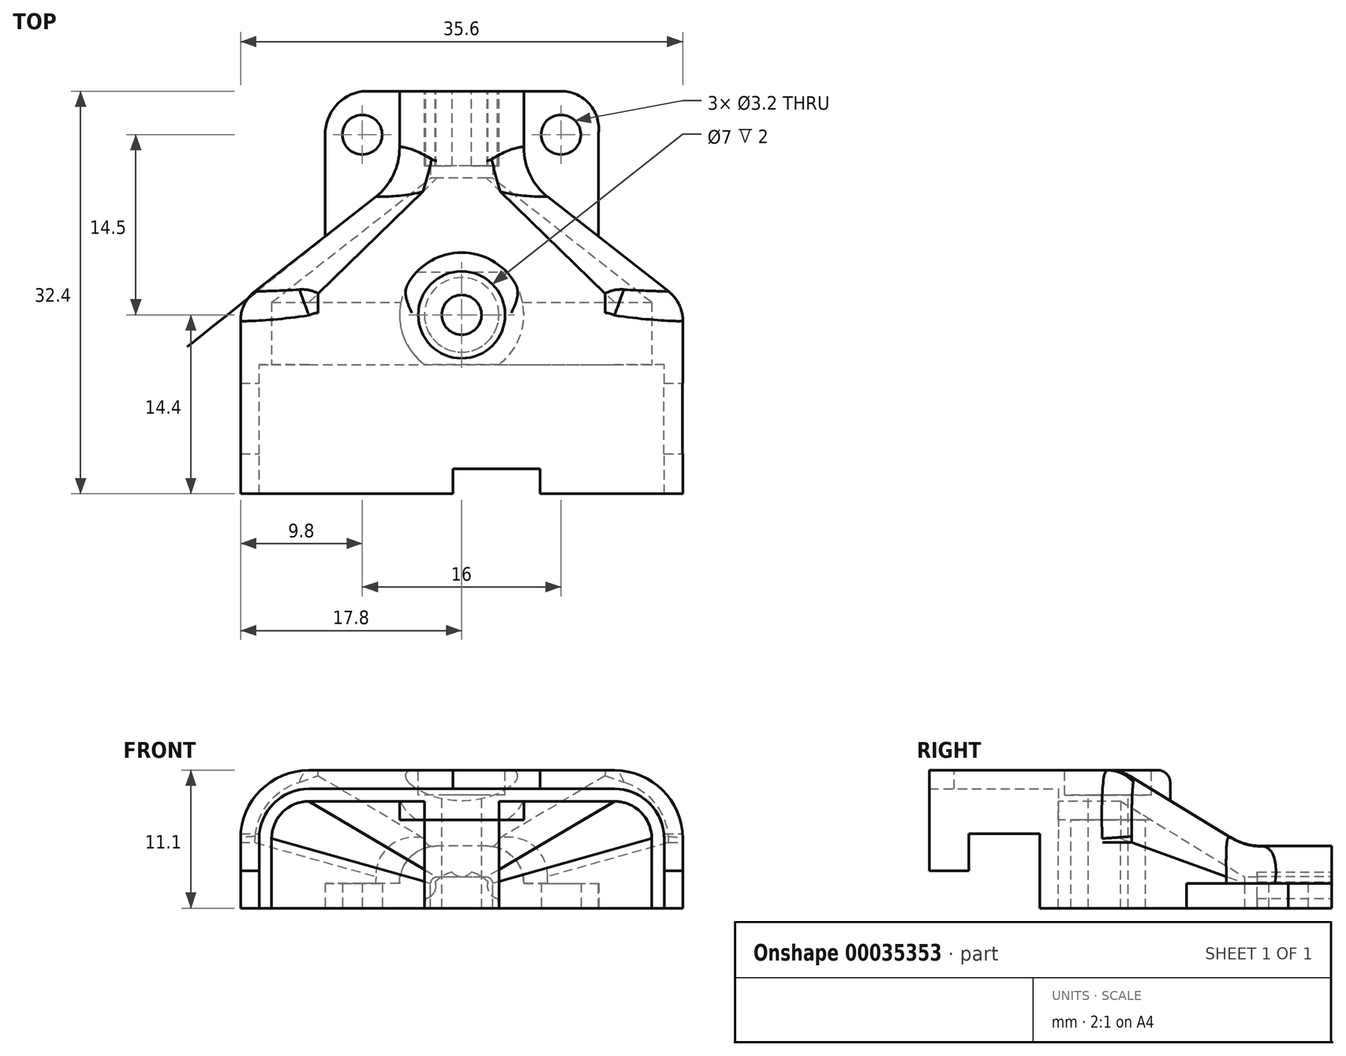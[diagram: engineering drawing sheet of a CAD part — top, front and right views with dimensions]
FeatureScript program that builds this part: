
annotation { "Feature Type Name" : "Feature", "Feature Type Description" : "" }
export const myFeature = defineFeature(function(context is Context, id is Id, definition is map)
    precondition{}
    {
        {
            var Q0;
            Q0=qCreatedBy(makeId("Front.planeOp"),FACE);
            var sketch = newSketch(context, id + "F0", { "sketchPlane" : qUnion([Q0])});
            skLineSegment(sketch, "E0", {"start": v(-16.3, 0) * mm, "end": v(-16.3, 5.6) * mm});
            skLineSegment(sketch, "E1", {"start": v(-12.3, 9.6) * mm, "end": v(0, 9.6) * mm});
            skPoint(sketch, "E2.visualSharp", {"position": v(-16.3, 9.6) * mm});
            skArc(sketch, "E2.filletArc", {"start": v(-12.3, 9.6) * mm, "mid": v(-15.13, 8.43) * mm, "end": v(-16.3, 5.6) * mm});
            skLineSegment(sketch, "E3.0", {"start": v(-12.3, 11.1) * mm, "end": v(0, 11.1) * mm});
            skArc(sketch, "E3.1", {"start": v(-12.3, 11.1) * mm, "mid": v(-16.19, 9.49) * mm, "end": v(-17.8, 5.6) * mm});
            skLineSegment(sketch, "E3.2", {"start": v(-17.8, 0) * mm, "end": v(-17.8, 5.6) * mm});
            skLineSegment(sketch, "E4", {"start": v(-17.8, 0) * mm, "end": v(-16.3, 0) * mm});
            skLineSegment(sketch, "E5.MirrorCS", {"start": v(12.3, 9.6) * mm, "end": v(0, 9.6) * mm});
            skLineSegment(sketch, "E6.MirrorCS", {"start": v(12.3, 11.1) * mm, "end": v(0, 11.1) * mm});
            skArc(sketch, "E7.MirrorCS", {"start": v(12.3, 11.1) * mm, "mid": v(16.19, 9.49) * mm, "end": v(17.8, 5.6) * mm});
            skArc(sketch, "E8.MirrorCS", {"start": v(12.3, 9.6) * mm, "mid": v(15.13, 8.43) * mm, "end": v(16.3, 5.6) * mm});
            skLineSegment(sketch, "E9.MirrorCS", {"start": v(16.3, 0) * mm, "end": v(16.3, 5.6) * mm});
            skLineSegment(sketch, "E10.MirrorCS", {"start": v(17.8, 0) * mm, "end": v(17.8, 5.6) * mm});
            skLineSegment(sketch, "E11.MirrorCS", {"start": v(17.8, 0) * mm, "end": v(16.3, 0) * mm});
            skSolve(sketch);
        }
        {
            var Q0;
            Q0=makeQuery(id+"F0.imprint","IMPRINT",FACE,{"disambiguationData":[TD([[makeQuery(id+"F0.imprint","IMPRINT",EDGE,{"derivedFrom":sQuery(id+"F0.wireOp",EDGE,"E0")}),1.0]])]});
            extrude(context, id + "F1", {"entities" : qUnion([Q0]), "depth" : 10.4 * mm});
        }
        {
            var Q0;
            Q0=makeQuery(id+"F1.opExtrude","CAP_FACE",FACE,{"disambiguationData":[OSD([sQuery(id+"F0.wireOp",EDGE,"E0"),sQuery(id+"F0.wireOp",EDGE,"E1"),sQuery(id+"F0.wireOp",EDGE,"E2.filletArc"),sQuery(id+"F0.wireOp",EDGE,"E3.0"),sQuery(id+"F0.wireOp",EDGE,"E3.1"),sQuery(id+"F0.wireOp",EDGE,"E3.2"),sQuery(id+"F0.wireOp",EDGE,"E4"),sQuery(id+"F0.wireOp",EDGE,"E5.MirrorCS"),sQuery(id+"F0.wireOp",EDGE,"E6.MirrorCS"),sQuery(id+"F0.wireOp",EDGE,"E7.MirrorCS"),sQuery(id+"F0.wireOp",EDGE,"E8.MirrorCS"),sQuery(id+"F0.wireOp",EDGE,"E9.MirrorCS"),sQuery(id+"F0.wireOp",EDGE,"E10.MirrorCS"),sQuery(id+"F0.wireOp",EDGE,"E11.MirrorCS")])],"isStart":true});
            var sketch = newSketch(context, id + "F2", { "sketchPlane" : qUnion([Q0])});
            skLineSegment(sketch, "E12.0", {"start": v(-15.3, 0) * mm, "end": v(-15.3, 5.6) * mm});
            skArc(sketch, "E12.1", {"start": v(-12.3, 8.6) * mm, "mid": v(-14.42, 7.72) * mm, "end": v(-15.3, 5.6) * mm});
            skLineSegment(sketch, "E12.2", {"start": v(12.3, 8.6) * mm, "end": v(-12.3, 8.6) * mm});
            skArc(sketch, "E12.3", {"start": v(12.3, 8.6) * mm, "mid": v(14.42, 7.72) * mm, "end": v(15.3, 5.6) * mm});
            skLineSegment(sketch, "E12.4", {"start": v(15.3, 0) * mm, "end": v(15.3, 5.6) * mm});
            skLineSegment(sketch, "E13", {"start": v(-15.3, 0) * mm, "end": v(-17.8, 0) * mm});
            skLineSegment(sketch, "E14", {"start": v(15.3, 0) * mm, "end": v(17.8, 0) * mm});
            skSolve(sketch);
        }
        {
            var Q0;
            {var subQ3=makeQuery(id+"F1.opExtrude","CAP_EDGE",EDGE,{"disambiguationData":[OSD([sQuery(id+"F0.wireOp",EDGE,"E0")])],"isStart":true});Q0=makeQuery(id+"F2.imprint","IMPRINT",FACE,{"disambiguationData":[TD([[makeQuery(id+"F2.imprint","IMPRINT",EDGE,{"derivedFrom":subQ3}),-1.0]])]});}
            var Q1;
            {var subQ5=sQuery(id+"F2.wireOp",EDGE,"E12.0");Q1=makeQuery(id+"F2.imprint","IMPRINT",FACE,{"disambiguationData":[TD([[makeQuery(id+"F2.imprint","IMPRINT",EDGE,{"derivedFrom":subQ5}),1.0]])]});}
            extrude(context, id + "F3", {"entities" : qUnion([Q0, Q1]), "operationType" : NewBodyOperationType.ADD, "depth" : 5 * mm});
        }
        {
            var Q0;
            Q0=makeQuery(id+"F3.opExtrude","CAP_FACE",FACE,{"disambiguationData":[OSD([sQuery(id+"F0.wireOp",EDGE,"E3.0"),sQuery(id+"F0.wireOp",EDGE,"E3.1"),sQuery(id+"F0.wireOp",EDGE,"E3.2"),sQuery(id+"F0.wireOp",EDGE,"E6.MirrorCS"),sQuery(id+"F0.wireOp",EDGE,"E7.MirrorCS"),sQuery(id+"F0.wireOp",EDGE,"E10.MirrorCS"),sQuery(id+"F2.wireOp",EDGE,"E12.0"),sQuery(id+"F2.wireOp",EDGE,"E12.1"),sQuery(id+"F2.wireOp",EDGE,"E12.2"),sQuery(id+"F2.wireOp",EDGE,"E12.3"),sQuery(id+"F2.wireOp",EDGE,"E12.4"),sQuery(id+"F2.wireOp",EDGE,"E13"),sQuery(id+"F2.wireOp",EDGE,"E14")])],"isStart":false});
            var sketch = newSketch(context, id + "F4", { "sketchPlane" : qUnion([Q0])});
            skLineSegment(sketch, "E15", {"start": v(0, 8.6) * mm, "end": v(0, 0) * mm, "construction": true});
            skLineSegment(sketch, "E16", {"start": v(-2.5, 0) * mm, "end": v(-5, 0) * mm});
            skLineSegment(sketch, "E17", {"start": v(-5, 0) * mm, "end": v(-5, 2) * mm});
            skLineSegment(sketch, "E18", {"start": v(-2, 5) * mm, "end": v(0, 5) * mm});
            skPoint(sketch, "E19.visualSharp", {"position": v(-5, 5) * mm});
            skArc(sketch, "E19.filletArc", {"start": v(-2, 5) * mm, "mid": v(-4.12, 4.12) * mm, "end": v(-5, 2) * mm});
            skLineSegment(sketch, "E20.0", {"start": v(-2, 2.5) * mm, "end": v(0, 2.5) * mm});
            skArc(sketch, "E20.1", {"start": v(-2, 2.5) * mm, "mid": v(-2.35, 2.35) * mm, "end": v(-2.5, 2) * mm});
            skLineSegment(sketch, "E20.2", {"start": v(-2.5, 0) * mm, "end": v(-2.5, 2) * mm});
            skLineSegment(sketch, "E21.MirrorCS", {"start": v(2, 2.5) * mm, "end": v(0, 2.5) * mm});
            skLineSegment(sketch, "E22.MirrorCS", {"start": v(2, 5) * mm, "end": v(0, 5) * mm});
            skArc(sketch, "E23.MirrorCS", {"start": v(2, 5) * mm, "mid": v(4.12, 4.12) * mm, "end": v(5, 2) * mm});
            skArc(sketch, "E24.MirrorCS", {"start": v(2, 2.5) * mm, "mid": v(2.35, 2.35) * mm, "end": v(2.5, 2) * mm});
            skLineSegment(sketch, "E25.MirrorCS", {"start": v(2.5, 0) * mm, "end": v(2.5, 2) * mm});
            skLineSegment(sketch, "E26.MirrorCS", {"start": v(5, 0) * mm, "end": v(5, 2) * mm});
            skLineSegment(sketch, "E27.MirrorCS", {"start": v(2.5, 0) * mm, "end": v(5, 0) * mm});
            skSolve(sketch);
        }
        {
            var Q0;
            Q0=makeQuery(id+"F4.imprint","IMPRINT",FACE,{"disambiguationData":[TD([[makeQuery(id+"F4.imprint","IMPRINT",EDGE,{"derivedFrom":sQuery(id+"F4.wireOp",EDGE,"E16")}),-1.0]])]});
            extrude(context, id + "F5", {"entities" : qUnion([Q0]), "operationType" : NewBodyOperationType.ADD, "depth" : 11 * mm, "hasSecondDirection" : true, "secondDirectionOppositeDirection" : false, "secondDirectionDepth" : 10 * mm});
        }
        {
            var Q0;
            Q0=makeQuery(id+"F3.opExtrude","CAP_FACE",FACE,{"disambiguationData":[OSD([sQuery(id+"F0.wireOp",EDGE,"E3.0"),sQuery(id+"F0.wireOp",EDGE,"E3.1"),sQuery(id+"F0.wireOp",EDGE,"E3.2"),sQuery(id+"F0.wireOp",EDGE,"E6.MirrorCS"),sQuery(id+"F0.wireOp",EDGE,"E7.MirrorCS"),sQuery(id+"F0.wireOp",EDGE,"E10.MirrorCS"),sQuery(id+"F2.wireOp",EDGE,"E12.0"),sQuery(id+"F2.wireOp",EDGE,"E12.1"),sQuery(id+"F2.wireOp",EDGE,"E12.2"),sQuery(id+"F2.wireOp",EDGE,"E12.3"),sQuery(id+"F2.wireOp",EDGE,"E12.4"),sQuery(id+"F2.wireOp",EDGE,"E13"),sQuery(id+"F2.wireOp",EDGE,"E14")])],"isStart":false});
            var Q1;
            Q1=makeQuery(id+"F5.opExtrude","CAP_FACE",FACE,{"disambiguationData":[OSD([sQuery(id+"F4.wireOp",EDGE,"E16"),sQuery(id+"F4.wireOp",EDGE,"E17"),sQuery(id+"F4.wireOp",EDGE,"E18"),sQuery(id+"F4.wireOp",EDGE,"E19.filletArc"),sQuery(id+"F4.wireOp",EDGE,"E20.0"),sQuery(id+"F4.wireOp",EDGE,"E20.1"),sQuery(id+"F4.wireOp",EDGE,"E20.2"),sQuery(id+"F4.wireOp",EDGE,"E21.MirrorCS"),sQuery(id+"F4.wireOp",EDGE,"E22.MirrorCS"),sQuery(id+"F4.wireOp",EDGE,"E23.MirrorCS"),sQuery(id+"F4.wireOp",EDGE,"E24.MirrorCS"),sQuery(id+"F4.wireOp",EDGE,"E25.MirrorCS"),sQuery(id+"F4.wireOp",EDGE,"E26.MirrorCS"),sQuery(id+"F4.wireOp",EDGE,"E27.MirrorCS")])],"isStart":true});
            loft(context, id + "F6", {"operationType" : NewBodyOperationType.ADD, "sheetProfilesArray" : [{ "sheetProfileEntities" : qUnion([Q0]) }, { "sheetProfileEntities" : qUnion([Q1]) }]});
        }
        {
            var Q0;
            Q0=makeQuery(id+"F5.opExtrude","CAP_FACE",FACE,{"disambiguationData":[OSD([sQuery(id+"F4.wireOp",EDGE,"E16"),sQuery(id+"F4.wireOp",EDGE,"E17"),sQuery(id+"F4.wireOp",EDGE,"E18"),sQuery(id+"F4.wireOp",EDGE,"E19.filletArc"),sQuery(id+"F4.wireOp",EDGE,"E20.0"),sQuery(id+"F4.wireOp",EDGE,"E20.1"),sQuery(id+"F4.wireOp",EDGE,"E20.2"),sQuery(id+"F4.wireOp",EDGE,"E21.MirrorCS"),sQuery(id+"F4.wireOp",EDGE,"E22.MirrorCS"),sQuery(id+"F4.wireOp",EDGE,"E23.MirrorCS"),sQuery(id+"F4.wireOp",EDGE,"E24.MirrorCS"),sQuery(id+"F4.wireOp",EDGE,"E25.MirrorCS"),sQuery(id+"F4.wireOp",EDGE,"E26.MirrorCS"),sQuery(id+"F4.wireOp",EDGE,"E27.MirrorCS")])],"isStart":false});
            var sketch = newSketch(context, id + "F7", { "sketchPlane" : qUnion([Q0])});
            skLineSegment(sketch, "E28", {"start": v(5, 0) * mm, "end": v(-5, 0) * mm});
            skSolve(sketch);
        }
        {
            var Q0;
            Q0=makeQuery(id+"F7.imprint","IMPRINT",FACE,{"disambiguationData":[TD([[makeQuery(id+"F7.imprint","IMPRINT",EDGE,{"derivedFrom":makeQuery(id+"F5.opExtrude","CAP_EDGE",EDGE,{"disambiguationData":[OSD([sQuery(id+"F4.wireOp",EDGE,"E20.1")])],"isStart":false})}),1.0]])]});
            var Q1;
            {var subQ3=makeQuery(id+"F5.opExtrude","CAP_EDGE",EDGE,{"disambiguationData":[OSD([sQuery(id+"F4.wireOp",EDGE,"E17")])],"isStart":false});Q1=makeQuery(id+"F7.imprint","IMPRINT",FACE,{"disambiguationData":[TD([[makeQuery(id+"F7.imprint","IMPRINT",EDGE,{"derivedFrom":subQ3}),-1.0]])]});}
            extrude(context, id + "F8", {"entities" : qUnion([Q0, Q1]), "operationType" : NewBodyOperationType.ADD, "depth" : 6 * mm});
        }
        {
            var Q0;
            Q0=makeQuery(id+"F8.opExtrude","CAP_FACE",FACE,{"disambiguationData":[OSD([sQuery(id+"F4.wireOp",EDGE,"E17"),sQuery(id+"F4.wireOp",EDGE,"E18"),sQuery(id+"F4.wireOp",EDGE,"E19.filletArc"),sQuery(id+"F4.wireOp",EDGE,"E22.MirrorCS"),sQuery(id+"F4.wireOp",EDGE,"E23.MirrorCS"),sQuery(id+"F4.wireOp",EDGE,"E26.MirrorCS"),sQuery(id+"F7.wireOp",EDGE,"E28")])],"isStart":false});
            var sketch = newSketch(context, id + "F9", { "sketchPlane" : qUnion([Q0])});
            skPoint(sketch, "E29.center.orphan", {"position": v(0, 0) * mm});
            skArc(sketch, "E30", {"start": v(3, 0) * mm, "mid": v(0, 3) * mm, "end": v(-3, 0) * mm});
            skLineSegment(sketch, "E31", {"start": v(3, 0) * mm, "end": v(-3, 0) * mm});
            skLineSegment(sketch, "E32", {"start": v(0, 0) * mm, "end": v(-2.9, 0.78) * mm, "construction": true});
            skLineSegment(sketch, "E33", {"start": v(0, 0) * mm, "end": v(-2.12, 2.12) * mm, "construction": true});
            skArc(sketch, "E34", {"start": v(-2.9, 0.78) * mm, "mid": v(-2.2, 1.27) * mm, "end": v(-2.12, 2.12) * mm});
            skArc(sketch, "E35.1.0", {"start": v(-0.78, 2.9) * mm, "mid": v(0, 2.55) * mm, "end": v(0.78, 2.9) * mm});
            skArc(sketch, "E35.2.0", {"start": v(2.12, 2.12) * mm, "mid": v(2.2, 1.27) * mm, "end": v(2.9, 0.78) * mm});
            skLineSegment(sketch, "E35.anchor2", {"start": v(0, 0) * mm, "end": v(2.12, 2.12) * mm, "construction": true});
            skSolve(sketch);
        }
        {
            var Q0;
            {var subQ5=sQuery(id+"F9.wireOp",EDGE,"E31");Q0=makeQuery(id+"F9.imprint","IMPRINT",FACE,{"disambiguationData":[TD([[makeQuery(id+"F9.imprint","IMPRINT",EDGE,{"derivedFrom":subQ5}),-1.0]])]});}
            extrude(context, id + "F10", {"entities" : qUnion([Q0]), "operationType" : NewBodyOperationType.REMOVE, "oppositeDirection" : true, "depth" : 6 * mm});
        }
        {
            var Q0;
            {var subQ0=sQuery(id+"F2.wireOp",EDGE,"E14");var subQ1=sQuery(id+"F4.wireOp",EDGE,"E27.MirrorCS");var subQ2=sQuery(id+"F0.wireOp",EDGE,"E3.2");var subQ3=sQuery(id+"F2.wireOp",EDGE,"E12.4");var subQ4=sQuery(id+"F4.wireOp",EDGE,"E25.MirrorCS");var subQ5=sQuery(id+"F4.wireOp",EDGE,"E26.MirrorCS");var subQ6=sQuery(id+"F2.wireOp",EDGE,"E13");var subQ7=sQuery(id+"F4.wireOp",EDGE,"E16");var subQ8=sQuery(id+"F0.wireOp",EDGE,"E10.MirrorCS");var subQ9=sQuery(id+"F2.wireOp",EDGE,"E12.0");var subQ10=sQuery(id+"F4.wireOp",EDGE,"E17");var subQ11=sQuery(id+"F7.wireOp",EDGE,"E28");Q0=makeQuery(id+"F10.boolean.opBoolean","SPLIT",FACE,{"disambiguationData":[TD([makeQuery(id+"F1.opExtrude","SWEPT_FACE",FACE,{"disambiguationData":[OSD([subQ2])]})])],"derivedFrom":makeQuery(id+"F8.boolean.opBoolean","MERGE",FACE,{"derivedFrom":[makeQuery(id+"F6.boolean.opBoolean","MERGE",FACE,{"derivedFrom":[makeQuery(id+"F3.boolean.opBoolean","MERGE",FACE,{"derivedFrom":[makeQuery(id+"F1.opExtrude","SWEPT_FACE",FACE,{"disambiguationData":[OSD([sQuery(id+"F0.wireOp",EDGE,"E4")])]}),makeQuery(id+"F3.opExtrude","SWEPT_FACE",FACE,{"disambiguationData":[OSD([subQ0])]})]}),makeQuery(id+"F5.opExtrude","SWEPT_FACE",FACE,{"disambiguationData":[OSD([subQ1])]}),makeQuery(id+"F6.opLoft","SWEPT_FACE",FACE,{"disambiguationData":[OSD([subQ2,subQ3,subQ0,subQ4,subQ5,subQ1])]})]}),makeQuery(id+"F6.boolean.opBoolean","MERGE",FACE,{"derivedFrom":[makeQuery(id+"F3.boolean.opBoolean","MERGE",FACE,{"derivedFrom":[makeQuery(id+"F1.opExtrude","SWEPT_FACE",FACE,{"disambiguationData":[OSD([sQuery(id+"F0.wireOp",EDGE,"E11.MirrorCS")])]}),makeQuery(id+"F3.opExtrude","SWEPT_FACE",FACE,{"disambiguationData":[OSD([subQ6])]})]}),makeQuery(id+"F5.opExtrude","SWEPT_FACE",FACE,{"disambiguationData":[OSD([subQ7])]}),makeQuery(id+"F6.opLoft","SWEPT_FACE",FACE,{"disambiguationData":[OSD([subQ8,subQ9,subQ6,subQ7,subQ10,sQuery(id+"F4.wireOp",EDGE,"E20.2")])]})]}),makeQuery(id+"F8.opExtrude","SWEPT_FACE",FACE,{"disambiguationData":[OSD([subQ11])]})]})});}
            var sketch = newSketch(context, id + "F11", { "sketchPlane" : qUnion([Q0])});
            skLineSegment(sketch, "E36", {"start": v(-5, -18.5) * mm, "end": v(-8, -18.5) * mm, "construction": true});
            skCircle(sketch, "E37", {"center": v(-8, -18.5) * mm, "radius": 1.6 * mm});
            skLineSegment(sketch, "E38", {"start": v(-5, -22) * mm, "end": v(-8, -22) * mm});
            skLineSegment(sketch, "E39", {"start": v(-8, -18.5) * mm, "end": v(-11, -18.5) * mm, "construction": true});
            skLineSegment(sketch, "E40", {"start": v(-11, -18.5) * mm, "end": v(-11, -8.36) * mm});
            skLineSegment(sketch, "E41", {"start": v(-5, -22) * mm, "end": v(-5, -13.05) * mm});
            skArc(sketch, "E42", {"start": v(-11, -18.5) * mm, "mid": v(-10.15, -20.8) * mm, "end": v(-8, -22) * mm});
            skSolve(sketch);
        }
        {
            var Q0;
            Q0=makeQuery(id+"F11.imprint","IMPRINT",FACE,{"disambiguationData":[TD([[makeQuery(id+"F11.imprint","IMPRINT",EDGE,{"derivedFrom":sQuery(id+"F11.wireOp",EDGE,"E37")}),-1.0]])]});
            var Q1;
            {var subQ0=sQuery(id+"F2.wireOp",EDGE,"E14");var subQ1=sQuery(id+"F4.wireOp",EDGE,"E27.MirrorCS");var subQ2=makeQuery(id+"F6.opLoft","SWEPT_EDGE",EDGE,{"disambiguationData":[OSD([sQuery(id+"F2.wireOp",EDGE,"E12.4"),subQ0,sQuery(id+"F4.wireOp",EDGE,"E25.MirrorCS"),subQ1])]});var subQ5=sQuery(id+"F11.wireOp",EDGE,"E40");var subQ6=makeQuery(id+"F11.imprint","INTERSECT",VERTEX,{"derivedFrom":[subQ2,subQ5]});Q1=makeQuery(id+"F11.imprint","IMPRINT",FACE,{"disambiguationData":[TD([[makeQuery(id+"F11.imprint","IMPRINT",EDGE,{"disambiguationData":[TD([[subQ6,1.0]])],"derivedFrom":subQ5}),-1.0]])]});}
            extrude(context, id + "F12", {"entities" : qUnion([Q0, Q1]), "operationType" : NewBodyOperationType.ADD, "oppositeDirection" : true, "depth" : 2 * mm});
        }
        {
            var Q0;
            {var subQ0=sQuery(id+"F2.wireOp",EDGE,"E14");var subQ1=sQuery(id+"F4.wireOp",EDGE,"E27.MirrorCS");var subQ2=sQuery(id+"F0.wireOp",EDGE,"E3.2");var subQ3=sQuery(id+"F2.wireOp",EDGE,"E12.4");var subQ4=sQuery(id+"F4.wireOp",EDGE,"E26.MirrorCS");var subQ5=sQuery(id+"F2.wireOp",EDGE,"E13");var subQ6=sQuery(id+"F4.wireOp",EDGE,"E16");var subQ7=sQuery(id+"F0.wireOp",EDGE,"E10.MirrorCS");var subQ8=sQuery(id+"F2.wireOp",EDGE,"E12.0");var subQ9=sQuery(id+"F4.wireOp",EDGE,"E17");var subQ10=sQuery(id+"F4.wireOp",EDGE,"E20.2");var subQ11=sQuery(id+"F7.wireOp",EDGE,"E28");Q0=makeQuery(id+"F10.boolean.opBoolean","SPLIT",FACE,{"disambiguationData":[TD([makeQuery(id+"F1.opExtrude","SWEPT_FACE",FACE,{"disambiguationData":[OSD([subQ7])]})])],"derivedFrom":makeQuery(id+"F8.boolean.opBoolean","MERGE",FACE,{"derivedFrom":[makeQuery(id+"F6.boolean.opBoolean","MERGE",FACE,{"derivedFrom":[makeQuery(id+"F3.boolean.opBoolean","MERGE",FACE,{"derivedFrom":[makeQuery(id+"F1.opExtrude","SWEPT_FACE",FACE,{"disambiguationData":[OSD([sQuery(id+"F0.wireOp",EDGE,"E4")])]}),makeQuery(id+"F3.opExtrude","SWEPT_FACE",FACE,{"disambiguationData":[OSD([subQ0])]})]}),makeQuery(id+"F5.opExtrude","SWEPT_FACE",FACE,{"disambiguationData":[OSD([subQ1])]}),makeQuery(id+"F6.opLoft","SWEPT_FACE",FACE,{"disambiguationData":[OSD([subQ2,subQ3,subQ0,sQuery(id+"F4.wireOp",EDGE,"E25.MirrorCS"),subQ4,subQ1])]})]}),makeQuery(id+"F6.boolean.opBoolean","MERGE",FACE,{"derivedFrom":[makeQuery(id+"F3.boolean.opBoolean","MERGE",FACE,{"derivedFrom":[makeQuery(id+"F1.opExtrude","SWEPT_FACE",FACE,{"disambiguationData":[OSD([sQuery(id+"F0.wireOp",EDGE,"E11.MirrorCS")])]}),makeQuery(id+"F3.opExtrude","SWEPT_FACE",FACE,{"disambiguationData":[OSD([subQ5])]})]}),makeQuery(id+"F5.opExtrude","SWEPT_FACE",FACE,{"disambiguationData":[OSD([subQ6])]}),makeQuery(id+"F6.opLoft","SWEPT_FACE",FACE,{"disambiguationData":[OSD([subQ7,subQ8,subQ5,subQ6,subQ9,subQ10])]})]}),makeQuery(id+"F8.opExtrude","SWEPT_FACE",FACE,{"disambiguationData":[OSD([subQ11])]})]})});}
            var sketch = newSketch(context, id + "F13", { "sketchPlane" : qUnion([Q0])});
            skLineSegment(sketch, "E43", {"start": v(5, -18.5) * mm, "end": v(11, -18.5) * mm, "construction": true});
            skPoint(sketch, "E43.endSnap0", {"position": v(5, -18.5) * mm});
            skCircle(sketch, "E44", {"center": v(8, -18.5) * mm, "radius": 1.6 * mm});
            skLineSegment(sketch, "E45", {"start": v(5, -22) * mm, "end": v(8, -22) * mm});
            skLineSegment(sketch, "E46", {"start": v(5, -22) * mm, "end": v(5, -13.05) * mm});
            skLineSegment(sketch, "E47", {"start": v(11, -18.5) * mm, "end": v(11, -8.36) * mm});
            skArc(sketch, "E48", {"start": v(8, -22) * mm, "mid": v(10.3, -20.94) * mm, "end": v(11, -18.5) * mm});
            skSolve(sketch);
        }
        {
            var Q0;
            Q0=makeQuery(id+"F13.imprint","IMPRINT",FACE,{"disambiguationData":[TD([[makeQuery(id+"F13.imprint","IMPRINT",EDGE,{"derivedFrom":sQuery(id+"F13.wireOp",EDGE,"E44")}),-1.0]])]});
            var Q1;
            {var subQ0=sQuery(id+"F2.wireOp",EDGE,"E13");var subQ1=sQuery(id+"F4.wireOp",EDGE,"E16");var subQ5=sQuery(id+"F13.wireOp",EDGE,"E46");var subQ7=makeQuery(id+"F6.opLoft","SWEPT_EDGE",EDGE,{"disambiguationData":[OSD([sQuery(id+"F0.wireOp",EDGE,"E10.MirrorCS"),subQ0,subQ1,sQuery(id+"F4.wireOp",EDGE,"E17")])]});var subQ9=makeQuery(id+"F13.imprint","INTERSECT",VERTEX,{"derivedFrom":[subQ7,subQ5]});Q1=makeQuery(id+"F13.imprint","IMPRINT",FACE,{"disambiguationData":[TD([[makeQuery(id+"F13.imprint","IMPRINT",EDGE,{"disambiguationData":[TD([[subQ9,-1.0]])],"derivedFrom":subQ5}),-1.0]])]});}
            extrude(context, id + "F14", {"entities" : qUnion([Q0, Q1]), "operationType" : NewBodyOperationType.ADD, "oppositeDirection" : true, "depth" : 2 * mm});
        }
        {
            var Q0;
            {var subQ0=sQuery(id+"F0.wireOp",EDGE,"E3.0");var subQ1=sQuery(id+"F0.wireOp",EDGE,"E6.MirrorCS");Q0=makeQuery(id+"F3.boolean.opBoolean","MERGE",FACE,{"derivedFrom":[makeQuery(id+"F1.opExtrude","SWEPT_FACE",FACE,{"disambiguationData":[OSD([subQ0,subQ1])]}),makeQuery(id+"F3.opExtrude","SWEPT_FACE",FACE,{"disambiguationData":[OSD([subQ0,subQ1])]})]});}
            var sketch = newSketch(context, id + "F15", { "sketchPlane" : qUnion([Q0])});
            skLineSegment(sketch, "E49", {"start": v(0, 0) * mm, "end": v(0, 4) * mm, "construction": true});
            skCircle(sketch, "E50", {"center": v(0, 4) * mm, "radius": 1.6 * mm});
            skSolve(sketch);
        }
        {
            var Q0;
            {var subQ0=sQuery(id+"F0.wireOp",EDGE,"E3.0");var subQ1=sQuery(id+"F0.wireOp",EDGE,"E6.MirrorCS");var subQ2=makeQuery(id+"F6.boolean.opBoolean","MERGE",EDGE,{"derivedFrom":[makeQuery(id+"F3.opExtrude","CAP_EDGE",EDGE,{"disambiguationData":[OSD([subQ0,subQ1])],"isStart":false}),makeQuery(id+"F6.opLoft","MID_CAP_EDGE",EDGE,{"disambiguationData":[OSD([subQ0,sQuery(id+"F0.wireOp",EDGE,"E3.1"),subQ1,sQuery(id+"F0.wireOp",EDGE,"E7.MirrorCS")])],"capPos":0.0})]});var subQ3=sQuery(id+"F15.wireOp",EDGE,"E50");var subQ5=makeQuery(id+"F15.imprint","INTERSECT",VERTEX,{"disambiguationData":[OD(0.0)],"derivedFrom":[subQ2,subQ3]});Q0=makeQuery(id+"F15.imprint","IMPRINT",FACE,{"disambiguationData":[TD([[makeQuery(id+"F15.imprint","IMPRINT",EDGE,{"disambiguationData":[TD([[subQ5,1.0]])],"derivedFrom":subQ3}),1.0]])]});}
            var Q1;
            {var subQ0=sQuery(id+"F0.wireOp",EDGE,"E3.0");var subQ1=sQuery(id+"F0.wireOp",EDGE,"E6.MirrorCS");var subQ2=makeQuery(id+"F6.boolean.opBoolean","MERGE",EDGE,{"derivedFrom":[makeQuery(id+"F3.opExtrude","CAP_EDGE",EDGE,{"disambiguationData":[OSD([subQ0,subQ1])],"isStart":false}),makeQuery(id+"F6.opLoft","MID_CAP_EDGE",EDGE,{"disambiguationData":[OSD([subQ0,sQuery(id+"F0.wireOp",EDGE,"E3.1"),subQ1,sQuery(id+"F0.wireOp",EDGE,"E7.MirrorCS")])],"capPos":0.0})]});var subQ3=sQuery(id+"F15.wireOp",EDGE,"E50");var subQ5=makeQuery(id+"F15.imprint","INTERSECT",VERTEX,{"disambiguationData":[OD(0.0)],"derivedFrom":[subQ2,subQ3]});Q1=makeQuery(id+"F15.imprint","IMPRINT",FACE,{"disambiguationData":[TD([[makeQuery(id+"F15.imprint","IMPRINT",EDGE,{"disambiguationData":[TD([[subQ5,-1.0]])],"derivedFrom":subQ3}),1.0]])]});}
            extrude(context, id + "F16", {"entities" : qUnion([Q0, Q1]), "operationType" : NewBodyOperationType.REMOVE, "oppositeDirection" : true, "depth" : 25 * mm});
        }
        {
            var Q0;
            {var subQ0=sQuery(id+"F0.wireOp",EDGE,"E3.0");var subQ1=sQuery(id+"F0.wireOp",EDGE,"E6.MirrorCS");Q0=makeQuery(id+"F3.boolean.opBoolean","MERGE",FACE,{"derivedFrom":[makeQuery(id+"F1.opExtrude","SWEPT_FACE",FACE,{"disambiguationData":[OSD([subQ0,subQ1])]}),makeQuery(id+"F3.opExtrude","SWEPT_FACE",FACE,{"disambiguationData":[OSD([subQ0,subQ1])]})]});}
            var sketch = newSketch(context, id + "F17", { "sketchPlane" : qUnion([Q0])});
            skArc(sketch, "E51", {"start": v(3, 0) * mm, "mid": v(0, 9) * mm, "end": v(-3, 0) * mm});
            skLineSegment(sketch, "E52", {"start": v(3, 0) * mm, "end": v(-3, 0) * mm});
            skCircle(sketch, "E53", {"center": v(0, 4) * mm, "radius": 1.6 * mm});
            skSolve(sketch);
        }
        {
            var Q0;
            {var subQ0=sQuery(id+"F0.wireOp",EDGE,"E3.0");var subQ1=sQuery(id+"F0.wireOp",EDGE,"E6.MirrorCS");var subQ2=sQuery(id+"F0.wireOp",EDGE,"E3.1");var subQ3=sQuery(id+"F0.wireOp",EDGE,"E7.MirrorCS");var subQ4=makeQuery(id+"F6.boolean.opBoolean","MERGE",EDGE,{"derivedFrom":[makeQuery(id+"F3.opExtrude","CAP_EDGE",EDGE,{"disambiguationData":[OSD([subQ0,subQ1])],"isStart":false}),makeQuery(id+"F6.opLoft","MID_CAP_EDGE",EDGE,{"disambiguationData":[OSD([subQ0,subQ2,subQ1,subQ3])],"capPos":0.0})]});var subQ13=makeQuery(id+"F16.boolean.opBoolean","SPLIT",EDGE,{"disambiguationData":[TD([makeQuery(id+"F1.opExtrude","SWEPT_FACE",FACE,{"disambiguationData":[OSD([subQ3])]})])],"derivedFrom":subQ4});var subQ14=sQuery(id+"F17.wireOp",EDGE,"E51");var subQ15=makeQuery(id+"F17.imprint","INTERSECT",VERTEX,{"derivedFrom":[subQ13,subQ14]});Q0=makeQuery(id+"F17.imprint","IMPRINT",FACE,{"disambiguationData":[TD([[makeQuery(id+"F17.imprint","IMPRINT",EDGE,{"disambiguationData":[TD([[subQ15,-1.0]])],"derivedFrom":subQ14}),1.0]])]});}
            var Q1;
            {var subQ21=sQuery(id+"F17.wireOp",EDGE,"E52");Q1=makeQuery(id+"F17.imprint","IMPRINT",FACE,{"disambiguationData":[TD([[makeQuery(id+"F17.imprint","IMPRINT",EDGE,{"derivedFrom":subQ21}),-1.0]])]});}
            extrude(context, id + "F18", {"entities" : qUnion([Q0, Q1]), "operationType" : NewBodyOperationType.ADD, "oppositeDirection" : true, "depth" : 4 * mm});
        }
        {
            var Q0;
            Q0=makeQuery(id+"F18.opExtrude","CAP_FACE",FACE,{"disambiguationData":[OSD([sQuery(id+"F17.wireOp",EDGE,"E51"),sQuery(id+"F17.wireOp",EDGE,"E52"),sQuery(id+"F17.wireOp",EDGE,"E53")])],"isStart":false});
            var sketch = newSketch(context, id + "F19", { "sketchPlane" : qUnion([Q0])});
            skCircle(sketch, "E54", {"center": v(0, -4) * mm, "radius": 3 * mm});
            skSolve(sketch);
        }
        {
            var Q0;
            Q0=makeQuery(id+"F19.imprint","IMPRINT",FACE,{"disambiguationData":[TD([[makeQuery(id+"F19.imprint","IMPRINT",EDGE,{"derivedFrom":sQuery(id+"F19.wireOp",EDGE,"E54")}),1.0]])]});
            extrude(context, id + "F20", {"entities" : qUnion([Q0]), "operationType" : NewBodyOperationType.ADD, "depth" : 7.1 * mm});
        }
        {
            var Q0;
            {var subQ0=sQuery(id+"F0.wireOp",EDGE,"E3.0");var subQ1=sQuery(id+"F0.wireOp",EDGE,"E6.MirrorCS");Q0=makeQuery(id+"F18.boolean.opBoolean","MERGE",FACE,{"derivedFrom":[makeQuery(id+"F3.boolean.opBoolean","MERGE",FACE,{"derivedFrom":[makeQuery(id+"F1.opExtrude","SWEPT_FACE",FACE,{"disambiguationData":[OSD([subQ0,subQ1])]}),makeQuery(id+"F3.opExtrude","SWEPT_FACE",FACE,{"disambiguationData":[OSD([subQ0,subQ1])]})]}),makeQuery(id+"F18.opExtrude","CAP_FACE",FACE,{"disambiguationData":[OSD([sQuery(id+"F17.wireOp",EDGE,"E51"),sQuery(id+"F17.wireOp",EDGE,"E52"),sQuery(id+"F17.wireOp",EDGE,"E53")])],"isStart":true})]});}
            var sketch = newSketch(context, id + "F21", { "sketchPlane" : qUnion([Q0])});
            skCircle(sketch, "E55", {"center": v(0, 4) * mm, "radius": 3.5 * mm});
            skSolve(sketch);
        }
        {
            var Q0;
            Q0=makeQuery(id+"F21.imprint","IMPRINT",FACE,{"disambiguationData":[TD([[makeQuery(id+"F21.imprint","IMPRINT",EDGE,{"derivedFrom":sQuery(id+"F21.wireOp",EDGE,"E55")}),1.0]])]});
            extrude(context, id + "F22", {"entities" : qUnion([Q0]), "operationType" : NewBodyOperationType.REMOVE, "oppositeDirection" : true, "depth" : 2 * mm});
        }
        {
            var Q0;
            Q0=makeQuery(id+"F18.opExtrude","CAP_EDGE",EDGE,{"disambiguationData":[OSD([sQuery(id+"F17.wireOp",EDGE,"E51")])],"isStart":true});
            fillet(context, id + "F23", {"entities" : qUnion([Q0]), "radius" : 1 * mm, "tangentPropagation" : true, "allowEdgeOverflow" : false});
        }
        {
            var Q0;
            {var subQ0=sQuery(id+"F4.wireOp",EDGE,"E19.filletArc");Q0=makeQuery(id+"F6.boolean.opBoolean","MERGE",EDGE,{"derivedFrom":[makeQuery(id+"F5.opExtrude","CAP_EDGE",EDGE,{"disambiguationData":[OSD([subQ0])],"isStart":true}),makeQuery(id+"F6.opLoft","MID_CAP_EDGE",EDGE,{"disambiguationData":[OSD([sQuery(id+"F4.wireOp",EDGE,"E17"),sQuery(id+"F4.wireOp",EDGE,"E18"),subQ0])],"capPos":1.0})]});}
            fillet(context, id + "F24", {"entities" : qUnion([Q0]), "radius" : 5 * mm, "tangentPropagation" : true, "allowEdgeOverflow" : false});
        }
        {
            var Q0;
            {var subQ0=sQuery(id+"F0.wireOp",EDGE,"E7.MirrorCS");Q0=makeQuery(id+"F6.boolean.opBoolean","MERGE",EDGE,{"derivedFrom":[makeQuery(id+"F3.opExtrude","CAP_EDGE",EDGE,{"disambiguationData":[OSD([subQ0])],"isStart":false}),makeQuery(id+"F6.opLoft","MID_CAP_EDGE",EDGE,{"disambiguationData":[OSD([sQuery(id+"F0.wireOp",EDGE,"E3.0"),sQuery(id+"F0.wireOp",EDGE,"E6.MirrorCS"),subQ0,sQuery(id+"F0.wireOp",EDGE,"E10.MirrorCS")])],"capPos":0.0})]});}
            var Q1;
            {var subQ0=sQuery(id+"F0.wireOp",EDGE,"E3.1");Q1=makeQuery(id+"F6.boolean.opBoolean","MERGE",EDGE,{"derivedFrom":[makeQuery(id+"F3.opExtrude","CAP_EDGE",EDGE,{"disambiguationData":[OSD([subQ0])],"isStart":false}),makeQuery(id+"F6.opLoft","MID_CAP_EDGE",EDGE,{"disambiguationData":[OSD([sQuery(id+"F0.wireOp",EDGE,"E3.0"),subQ0,sQuery(id+"F0.wireOp",EDGE,"E3.2"),sQuery(id+"F0.wireOp",EDGE,"E6.MirrorCS")])],"capPos":0.0})]});}
            fillet(context, id + "F25", {"entities" : qUnion([Q0, Q1]), "radius" : 3 * mm, "tangentPropagation" : true, "allowEdgeOverflow" : false});
        }
        {
            var Q0;
            {var subQ0=sQuery(id+"F0.wireOp",EDGE,"E3.0");var subQ1=sQuery(id+"F0.wireOp",EDGE,"E6.MirrorCS");Q0=makeQuery(id+"F18.boolean.opBoolean","MERGE",FACE,{"derivedFrom":[makeQuery(id+"F3.boolean.opBoolean","MERGE",FACE,{"derivedFrom":[makeQuery(id+"F1.opExtrude","SWEPT_FACE",FACE,{"disambiguationData":[OSD([subQ0,subQ1])]}),makeQuery(id+"F3.opExtrude","SWEPT_FACE",FACE,{"disambiguationData":[OSD([subQ0,subQ1])]})]}),makeQuery(id+"F18.opExtrude","CAP_FACE",FACE,{"disambiguationData":[OSD([sQuery(id+"F17.wireOp",EDGE,"E51"),sQuery(id+"F17.wireOp",EDGE,"E52"),sQuery(id+"F17.wireOp",EDGE,"E53")])],"isStart":true})]});}
            var sketch = newSketch(context, id + "F26", { "sketchPlane" : qUnion([Q0])});
            skLineSegment(sketch, "E56", {"start": v(12.3, -10.4) * mm, "end": v(-0.7, -10.4) * mm, "construction": true});
            skLineSegment(sketch, "E57.bottom", {"start": v(-0.7, -10.4) * mm, "end": v(6.3, -10.4) * mm});
            skLineSegment(sketch, "E57.top", {"start": v(-0.7, -8.4) * mm, "end": v(6.3, -8.4) * mm});
            skLineSegment(sketch, "E57.left", {"start": v(-0.7, -10.4) * mm, "end": v(-0.7, -8.4) * mm});
            skLineSegment(sketch, "E57.right", {"start": v(6.3, -10.4) * mm, "end": v(6.3, -8.4) * mm});
            skSolve(sketch);
        }
        {
            var Q0;
            Q0=makeQuery(id+"F26.imprint","IMPRINT",FACE,{"disambiguationData":[TD([[makeQuery(id+"F26.imprint","IMPRINT",EDGE,{"derivedFrom":sQuery(id+"F26.wireOp",EDGE,"E57.bottom")}),-1.0]])]});
            extrude(context, id + "F27", {"entities" : qUnion([Q0]), "operationType" : NewBodyOperationType.REMOVE, "oppositeDirection" : true, "depth" : 25 * mm});
        }
        {
            var Q0;
            {var subQ0=sQuery(id+"F0.wireOp",EDGE,"E10.MirrorCS");Q0=makeQuery(id+"F3.boolean.opBoolean","MERGE",FACE,{"derivedFrom":[makeQuery(id+"F1.opExtrude","SWEPT_FACE",FACE,{"disambiguationData":[OSD([subQ0])]}),makeQuery(id+"F3.opExtrude","SWEPT_FACE",FACE,{"disambiguationData":[OSD([subQ0])]})]});}
            var sketch = newSketch(context, id + "F28", { "sketchPlane" : qUnion([Q0])});
            skLineSegment(sketch, "E58", {"start": v(0, 0) * mm, "end": v(-1.5, 0) * mm, "construction": true});
            skLineSegment(sketch, "E59.bottom", {"start": v(-1.5, 0) * mm, "end": v(-7.2, 0) * mm});
            skLineSegment(sketch, "E59.top", {"start": v(-1.5, 6) * mm, "end": v(-7.2, 6) * mm});
            skLineSegment(sketch, "E59.left", {"start": v(-1.5, 0) * mm, "end": v(-1.5, 6) * mm});
            skLineSegment(sketch, "E59.right", {"start": v(-7.2, 0) * mm, "end": v(-7.2, 6) * mm});
            skLineSegment(sketch, "E60.bottom", {"start": v(-7.2, 0) * mm, "end": v(-10.4, 0) * mm});
            skLineSegment(sketch, "E60.top", {"start": v(-7.2, 3) * mm, "end": v(-10.4, 3) * mm});
            skLineSegment(sketch, "E60.left", {"start": v(-7.2, 0) * mm, "end": v(-7.2, 3) * mm});
            skLineSegment(sketch, "E60.right", {"start": v(-10.4, 0) * mm, "end": v(-10.4, 3) * mm});
            skSolve(sketch);
        }
        {
            var Q0;
            {var subQ8=sQuery(id+"F28.wireOp",EDGE,"E59.bottom");Q0=makeQuery(id+"F28.imprint","IMPRINT",FACE,{"disambiguationData":[TD([[makeQuery(id+"F28.imprint","IMPRINT",EDGE,{"derivedFrom":subQ8}),1.0]])]});}
            var Q1;
            Q1=makeQuery(id+"F28.imprint","IMPRINT",FACE,{"disambiguationData":[TD([[makeQuery(id+"F28.imprint","IMPRINT",EDGE,{"derivedFrom":sQuery(id+"F28.wireOp",EDGE,"E60.bottom")}),1.0]])]});
            var Q2;
            {var subQ7=sQuery(id+"F28.wireOp",EDGE,"E59.top");Q2=makeQuery(id+"F28.imprint","IMPRINT",FACE,{"disambiguationData":[TD([[makeQuery(id+"F28.imprint","IMPRINT",EDGE,{"derivedFrom":subQ7}),1.0]])]});}
            extrude(context, id + "F29", {"entities" : qUnion([Q0, Q1, Q2]), "operationType" : NewBodyOperationType.REMOVE, "endBound" : BoundingType.THROUGH_ALL, "oppositeDirection" : true, "depth" : 25 * mm});
        }
    });
